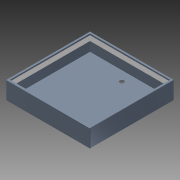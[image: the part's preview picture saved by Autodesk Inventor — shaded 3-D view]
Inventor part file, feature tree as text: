
AUTODESK INVENTOR PART (.ipt)
format: ipt  version: 2014 (Build 180170000, 170)  size: 188,416 bytes
history: native  units: in
note: dims shown in document units (in); Inventor stores cm internally (conversion verified against a paired STEP export)
features: extrude x10, sketch x8, projected_geometry x3, thread x2, plane x1, fillet x1, mirror x1
ambient origin geometry x8: Origin, YZ Plane, XZ Plane, XY Plane, X Axis, Y Axis, Z Axis, Center Point
bodies: Solid1 (feature_tree)
feature tree (26):
  extrude  "Extrusion1"  Depth=25.997in
  extrude  "Extrusion2"  Depth=0.0625in
  extrude  "Extrusion3"  Depth=5.375in TaperAngle=0.0deg
  plane  "Work Plane1"
  extrude  "Extrusion4"  [1 undecoded]
  fillet  "Fillet1"  Radius=0.0625in
  extrude  "Extrusion12"  Depth=1.315in
  sketch  "Sketch5"  dims[d74=2.25in d75=1.315in]
  extrude  "Extrusion5"  Depth=1.0in TaperAngle=0.0deg
  extrude  "Extrusion6"  Depth=1.0in
  extrude  "Extrusion7"  Depth=1.0in TaperAngle=0.0deg
  extrude  "Extrusion8"  Depth=1.0in TaperAngle=0.0deg
  thread  "Thread1"  [1 undecoded]
  thread  "Thread2"  [1 undecoded]
  extrude  "Extrusion9"  Depth=1.0in
  mirror  "Mirror1"
  sketch  "Sketch1"  dims[d0=25.997in d2=25.997in]
  sketch  "Sketch2"  dims[d5=0.0625in d6=0.0in d7=0.0625in]
  projected_geometry  "Projected Loop1"
  sketch  "Sketch3"  dims[d8=0.0625in d9=5.375in d10=0.0in]
  sketch  "Sketch4"  dims[d11=0.0625in d12=0.0in d13=-1.0in d16=0.0625in d17=0.0in]
  projected_geometry  "Projected Loop2"
  projected_geometry  "Projected Loop3"
  sketch  "Sketch6"  dims[d77=1.0in d78=0.0in d79=9.0in d80=0.0in]
  sketch  "Sketch7"  dims[d81=1.0625in d82=0.0in d83=1.0in]
  sketch  "Sketch11"  dims[d84=9.0in d85=0.0in d86=0.794in d87=0.0in d88=0.392in d89=0.0in d90=0.125in d91=0.25in d95=2.313in d96=0.625in d97=1.0in d98=0.0in d121=1.625in d122=1.625in d123=0.625in d124=0.625in d130=1.315in d131=3.0in d132=1.0in d133=0.0in]
note: 3 required parameter values undecoded (feature->parameter linkage not recoverable at this tier; creation-order binding heuristic only, values carry confidence <= 0.55)
